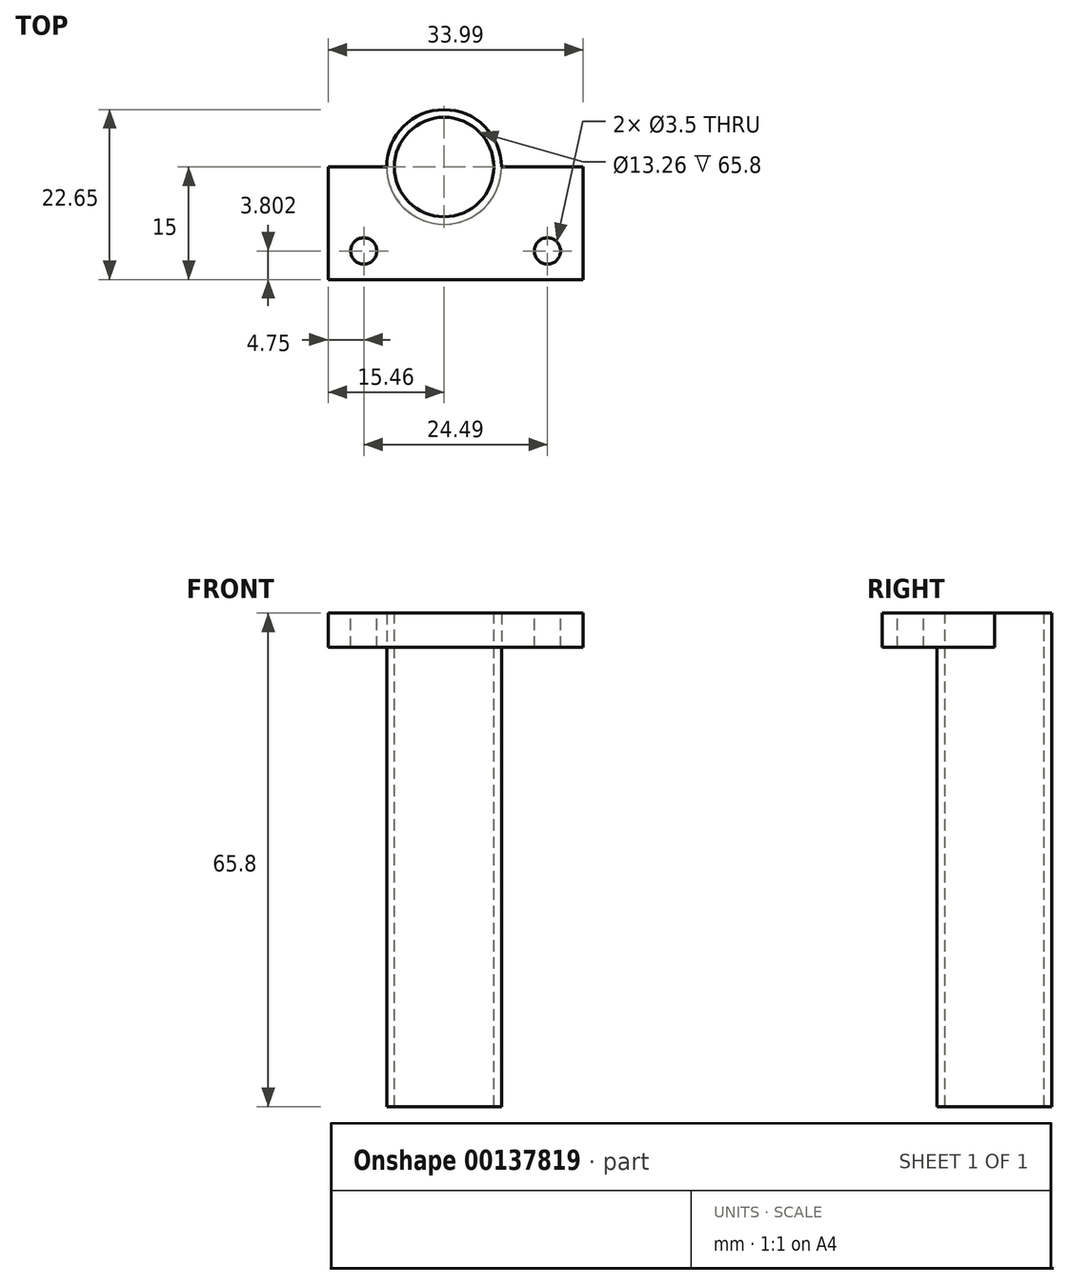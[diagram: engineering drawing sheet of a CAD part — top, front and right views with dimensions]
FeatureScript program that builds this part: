
annotation { "Feature Type Name" : "Feature", "Feature Type Description" : "" }
export const myFeature = defineFeature(function(context is Context, id is Id, definition is map)
    precondition{}
    {
        {
            var Q0;
            Q0=qCreatedBy(makeId("Top.planeOp"),FACE);
            var sketch = newSketch(context, id + "F0", { "sketchPlane" : qUnion([Q0])});
            skCircle(sketch, "E0", {"center": v(0, 0) * mm, "radius": 7.65 * mm});
            skSolve(sketch);
        }
        {
            var Q0;
            Q0 = qSketchRegion(id + "F0", true);
            extrude(context, id + "F1", {"entities" : qUnion([Q0]), "depth" : 65.8 * mm});
        }
        {
            var Q0;
            Q0=makeQuery(id+"F1.opExtrude","CAP_FACE",FACE,{"disambiguationData":[OSD([sQuery(id+"F0.wireOp",EDGE,"E0")])],"isStart":false});
            var sketch = newSketch(context, id + "F2", { "sketchPlane" : qUnion([Q0])});
            skCircle(sketch, "E1", {"center": v(0, 0) * mm, "radius": 6.63 * mm});
            skSolve(sketch);
        }
        {
            var Q0;
            Q0 = qSketchRegion(id + "F2", true);
            extrude(context, id + "F3", {"entities" : qUnion([Q0]), "operationType" : NewBodyOperationType.REMOVE, "endBound" : BoundingType.THROUGH_ALL, "oppositeDirection" : true, "depth" : 25 * mm});
        }
        {
            var Q0;
            Q0=makeQuery(id+"F1.opExtrude","CAP_FACE",FACE,{"disambiguationData":[OSD([sQuery(id+"F0.wireOp",EDGE,"E0")])],"isStart":false});
            var sketch = newSketch(context, id + "F4", { "sketchPlane" : qUnion([Q0])});
            skLineSegment(sketch, "E2.bottom", {"start": v(-15.46, 0) * mm, "end": v(18.53, 0) * mm});
            skLineSegment(sketch, "E2.top", {"start": v(-15.46, -15) * mm, "end": v(18.53, -15) * mm});
            skLineSegment(sketch, "E2.left", {"start": v(-15.46, 0) * mm, "end": v(-15.46, -15) * mm});
            skLineSegment(sketch, "E2.right", {"start": v(18.53, 0) * mm, "end": v(18.53, -15) * mm});
            skSolve(sketch);
        }
        {
            var Q0;
            Q0 = qSketchRegion(id + "F4", true);
            extrude(context, id + "F5", {"entities" : qUnion([Q0]), "operationType" : NewBodyOperationType.ADD, "oppositeDirection" : true, "depth" : 4.56 * mm});
        }
        {
            var Q0;
            Q0=makeQuery(id+"F5.boolean.opBoolean","MERGE",FACE,{"derivedFrom":[makeQuery(id+"F1.opExtrude","CAP_FACE",FACE,{"disambiguationData":[OSD([sQuery(id+"F0.wireOp",EDGE,"E0")])],"isStart":false}),makeQuery(id+"F5.opExtrude","CAP_FACE",FACE,{"disambiguationData":[OSD([sQuery(id+"F4.wireOp",EDGE,"E2.bottom"),sQuery(id+"F4.wireOp",EDGE,"E2.top"),sQuery(id+"F4.wireOp",EDGE,"E2.left"),sQuery(id+"F4.wireOp",EDGE,"E2.right")])],"isStart":true})]});
            var sketch = newSketch(context, id + "F6", { "sketchPlane" : qUnion([Q0])});
            skCircle(sketch, "E3", {"center": v(0, 0) * mm, "radius": 6.63 * mm});
            skSolve(sketch);
        }
        {
            var Q0;
            Q0 = qSketchRegion(id + "F6", true);
            extrude(context, id + "F7", {"entities" : qUnion([Q0]), "operationType" : NewBodyOperationType.REMOVE, "endBound" : BoundingType.THROUGH_ALL, "oppositeDirection" : true, "depth" : 25 * mm});
        }
        {
            var Q0;
            Q0=makeQuery(id+"F5.boolean.opBoolean","MERGE",FACE,{"derivedFrom":[makeQuery(id+"F1.opExtrude","CAP_FACE",FACE,{"disambiguationData":[OSD([sQuery(id+"F0.wireOp",EDGE,"E0")])],"isStart":false}),makeQuery(id+"F5.opExtrude","CAP_FACE",FACE,{"disambiguationData":[OSD([sQuery(id+"F4.wireOp",EDGE,"E2.bottom"),sQuery(id+"F4.wireOp",EDGE,"E2.top"),sQuery(id+"F4.wireOp",EDGE,"E2.left"),sQuery(id+"F4.wireOp",EDGE,"E2.right")])],"isStart":true})]});
            var sketch = newSketch(context, id + "F8", { "sketchPlane" : qUnion([Q0])});
            skCircle(sketch, "E4", {"center": v(-10.71, -11.2) * mm, "radius": 1.75 * mm});
            skCircle(sketch, "E5", {"center": v(13.78, -11.2) * mm, "radius": 1.75 * mm});
            skSolve(sketch);
        }
        {
            var Q0;
            Q0 = qSketchRegion(id + "F8", true);
            extrude(context, id + "F9", {"entities" : qUnion([Q0]), "operationType" : NewBodyOperationType.REMOVE, "endBound" : BoundingType.THROUGH_ALL, "oppositeDirection" : true, "depth" : 25 * mm});
        }
    });
